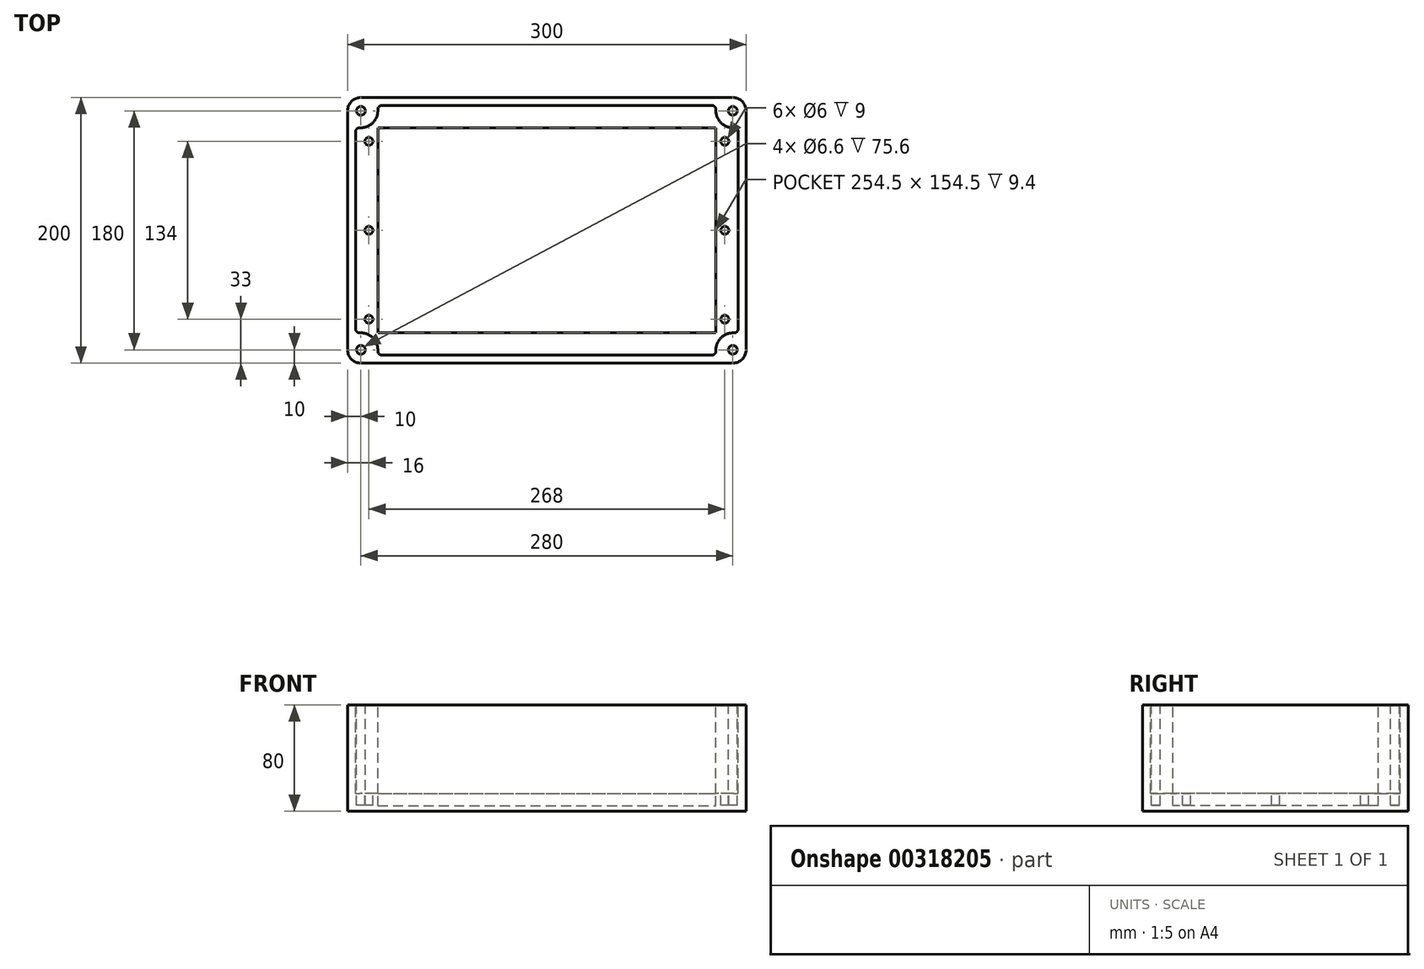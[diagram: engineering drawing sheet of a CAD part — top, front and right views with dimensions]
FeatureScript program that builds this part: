
annotation { "Feature Type Name" : "Feature", "Feature Type Description" : "" }
export const myFeature = defineFeature(function(context is Context, id is Id, definition is map)
    precondition{}
    {
        {
            var Q0;
            Q0=qCreatedBy(makeId("Top.planeOp"),FACE);
            var sketch = newSketch(context, id + "F0", { "sketchPlane" : qUnion([Q0])});
            skLineSegment(sketch, "E0.bottom", {"start": v(10, 0) * mm, "end": v(290, 0) * mm});
            skLineSegment(sketch, "E0.top", {"start": v(10, -200) * mm, "end": v(290, -200) * mm});
            skLineSegment(sketch, "E0.left", {"start": v(0, -10) * mm, "end": v(0, -190) * mm});
            skLineSegment(sketch, "E0.right", {"start": v(300, -10) * mm, "end": v(300, -190) * mm});
            skLineSegment(sketch, "E1.bottom", {"start": v(10, -10) * mm, "end": v(290, -10) * mm, "construction": true});
            skLineSegment(sketch, "E1.top", {"start": v(10, -190) * mm, "end": v(290, -190) * mm, "construction": true});
            skLineSegment(sketch, "E1.left", {"start": v(10, -10) * mm, "end": v(10, -190) * mm, "construction": true});
            skLineSegment(sketch, "E1.right", {"start": v(290, -10) * mm, "end": v(290, -190) * mm, "construction": true});
            skPoint(sketch, "E2.visualSharp", {"position": v(0, 0) * mm});
            skArc(sketch, "E2.filletArc", {"start": v(10, 0) * mm, "mid": v(2.93, -2.93) * mm, "end": v(0, -10) * mm});
            skPoint(sketch, "E3.visualSharp", {"position": v(300, 0) * mm});
            skArc(sketch, "E3.filletArc", {"start": v(300, -10) * mm, "mid": v(297.07, -2.93) * mm, "end": v(290, 0) * mm});
            skPoint(sketch, "E4.visualSharp", {"position": v(300, -200) * mm});
            skArc(sketch, "E4.filletArc", {"start": v(290, -200) * mm, "mid": v(297.07, -197.07) * mm, "end": v(300, -190) * mm});
            skPoint(sketch, "E5.visualSharp", {"position": v(0, -200) * mm});
            skArc(sketch, "E5.filletArc", {"start": v(0, -190) * mm, "mid": v(2.93, -197.07) * mm, "end": v(10, -200) * mm});
            skSolve(sketch);
        }
        {
            var Q0;
            Q0=makeQuery(id+"F0.imprint","IMPRINT",FACE,{"disambiguationData":[TD([[makeQuery(id+"F0.imprint","IMPRINT",EDGE,{"derivedFrom":sQuery(id+"F0.wireOp",EDGE,"E0.bottom")}),-1.0]])]});
            extrude(context, id + "F1", {"entities" : qUnion([Q0]), "depth" : 80 * mm});
        }
        {
            var Q0;
            Q0=makeQuery(id+"F1.opExtrude","CAP_FACE",FACE,{"disambiguationData":[OSD([sQuery(id+"F0.wireOp",EDGE,"E0.bottom"),sQuery(id+"F0.wireOp",EDGE,"E0.top"),sQuery(id+"F0.wireOp",EDGE,"E0.left"),sQuery(id+"F0.wireOp",EDGE,"E0.right")])],"isStart":false});
            var sketch = newSketch(context, id + "F2", { "sketchPlane" : qUnion([Q0])});
            skLineSegment(sketch, "E6.bottom", {"start": v(10, -10) * mm, "end": v(290, -10) * mm, "construction": true});
            skLineSegment(sketch, "E6.top", {"start": v(10, -190) * mm, "end": v(290, -190) * mm, "construction": true});
            skLineSegment(sketch, "E6.left", {"start": v(10, -10) * mm, "end": v(10, -190) * mm, "construction": true});
            skLineSegment(sketch, "E6.right", {"start": v(290, -10) * mm, "end": v(290, -190) * mm, "construction": true});
            skCircle(sketch, "E7", {"center": v(10, -10) * mm, "radius": 3.3 * mm});
            skCircle(sketch, "E8", {"center": v(290, -10) * mm, "radius": 3.3 * mm});
            skCircle(sketch, "E9", {"center": v(290, -190) * mm, "radius": 3.3 * mm});
            skCircle(sketch, "E10", {"center": v(10, -190) * mm, "radius": 3.3 * mm});
            skLineSegment(sketch, "E11.bottom", {"start": v(6, -6) * mm, "end": v(294, -6) * mm});
            skLineSegment(sketch, "E11.top", {"start": v(6, -194) * mm, "end": v(294, -194) * mm});
            skLineSegment(sketch, "E11.left", {"start": v(6, -6) * mm, "end": v(6, -194) * mm});
            skLineSegment(sketch, "E11.right", {"start": v(294, -6) * mm, "end": v(294, -194) * mm});
            skLineSegment(sketch, "E12.bottom", {"start": v(16, -33) * mm, "end": v(284, -33) * mm, "construction": true});
            skLineSegment(sketch, "E12.top", {"start": v(16, -167) * mm, "end": v(284, -167) * mm, "construction": true});
            skLineSegment(sketch, "E12.left", {"start": v(16, -33) * mm, "end": v(16, -167) * mm, "construction": true});
            skLineSegment(sketch, "E12.right", {"start": v(284, -33) * mm, "end": v(284, -167) * mm, "construction": true});
            skLineSegment(sketch, "E13", {"start": v(16, -100) * mm, "end": v(284, -100) * mm, "construction": true});
            skCircle(sketch, "E14", {"center": v(16, -33) * mm, "radius": 3 * mm});
            skCircle(sketch, "E15", {"center": v(16, -100) * mm, "radius": 3 * mm});
            skCircle(sketch, "E16", {"center": v(16, -167) * mm, "radius": 3 * mm});
            skCircle(sketch, "E17", {"center": v(284, -33) * mm, "radius": 3 * mm});
            skCircle(sketch, "E18", {"center": v(284, -100) * mm, "radius": 3 * mm});
            skCircle(sketch, "E19", {"center": v(284, -167) * mm, "radius": 3 * mm});
            skSolve(sketch);
        }
        {
            var Q0;
            Q0=makeQuery(id+"F2.imprint","IMPRINT",FACE,{"disambiguationData":[TD([[makeQuery(id+"F2.imprint","IMPRINT",EDGE,{"derivedFrom":sQuery(id+"F2.wireOp",EDGE,"E7")}),1.0]])]});
            var Q1;
            Q1=makeQuery(id+"F2.imprint","IMPRINT",FACE,{"disambiguationData":[TD([[makeQuery(id+"F2.imprint","IMPRINT",EDGE,{"derivedFrom":sQuery(id+"F2.wireOp",EDGE,"E10")}),1.0]])]});
            var Q2;
            Q2=makeQuery(id+"F2.imprint","IMPRINT",FACE,{"disambiguationData":[TD([[makeQuery(id+"F2.imprint","IMPRINT",EDGE,{"derivedFrom":sQuery(id+"F2.wireOp",EDGE,"E9")}),1.0]])]});
            var Q3;
            Q3=makeQuery(id+"F2.imprint","IMPRINT",FACE,{"disambiguationData":[TD([[makeQuery(id+"F2.imprint","IMPRINT",EDGE,{"derivedFrom":sQuery(id+"F2.wireOp",EDGE,"E8")}),1.0]])]});
            var Q4;
            Q4=makeQuery(id+"F2.imprint","IMPRINT",FACE,{"disambiguationData":[TD([[makeQuery(id+"F2.imprint","IMPRINT",EDGE,{"derivedFrom":sQuery(id+"F2.wireOp",EDGE,"E14")}),1.0]])]});
            var Q5;
            Q5=makeQuery(id+"F2.imprint","IMPRINT",FACE,{"disambiguationData":[TD([[makeQuery(id+"F2.imprint","IMPRINT",EDGE,{"derivedFrom":sQuery(id+"F2.wireOp",EDGE,"E15")}),1.0]])]});
            var Q6;
            Q6=makeQuery(id+"F2.imprint","IMPRINT",FACE,{"disambiguationData":[TD([[makeQuery(id+"F2.imprint","IMPRINT",EDGE,{"derivedFrom":sQuery(id+"F2.wireOp",EDGE,"E16")}),1.0]])]});
            var Q7;
            Q7=makeQuery(id+"F2.imprint","IMPRINT",FACE,{"disambiguationData":[TD([[makeQuery(id+"F2.imprint","IMPRINT",EDGE,{"derivedFrom":sQuery(id+"F2.wireOp",EDGE,"E18")}),1.0]])]});
            var Q8;
            Q8=makeQuery(id+"F2.imprint","IMPRINT",FACE,{"disambiguationData":[TD([[makeQuery(id+"F2.imprint","IMPRINT",EDGE,{"derivedFrom":sQuery(id+"F2.wireOp",EDGE,"E17")}),1.0]])]});
            var Q9;
            Q9=makeQuery(id+"F2.imprint","IMPRINT",FACE,{"disambiguationData":[TD([[makeQuery(id+"F2.imprint","IMPRINT",EDGE,{"derivedFrom":sQuery(id+"F2.wireOp",EDGE,"E19")}),1.0]])]});
            var Q10;
            Q10=sQuery(id+"F2.wireOp",EDGE,"E17");
            var Q11;
            Q11=sQuery(id+"F2.wireOp",EDGE,"E8");
            var Q12;
            Q12=sQuery(id+"F2.wireOp",EDGE,"E18");
            var Q13;
            Q13=sQuery(id+"F2.wireOp",EDGE,"E19");
            var Q14;
            Q14=sQuery(id+"F2.wireOp",EDGE,"E9");
            var Q15;
            Q15=sQuery(id+"F2.wireOp",EDGE,"E16");
            var Q16;
            Q16=sQuery(id+"F2.wireOp",EDGE,"E10");
            var Q17;
            Q17=sQuery(id+"F2.wireOp",EDGE,"E15");
            var Q18;
            Q18=sQuery(id+"F2.wireOp",EDGE,"E14");
            var Q19;
            Q19=sQuery(id+"F2.wireOp",EDGE,"E7");
            extrude(context, id + "F3", {"entities" : qUnion([Q0, Q1, Q2, Q3, Q4, Q5, Q6, Q7, Q8, Q9]), "operationType" : NewBodyOperationType.REMOVE, "surfaceEntities" : qUnion([Q10, Q11, Q12, Q13, Q14, Q15, Q16, Q17, Q18, Q19]), "oppositeDirection" : true, "depth" : 75.6 * mm});
        }
        {
            var Q0;
            Q0=makeQuery(id+"F1.opExtrude","CAP_FACE",FACE,{"disambiguationData":[OSD([sQuery(id+"F0.wireOp",EDGE,"E0.bottom"),sQuery(id+"F0.wireOp",EDGE,"E0.top"),sQuery(id+"F0.wireOp",EDGE,"E0.left"),sQuery(id+"F0.wireOp",EDGE,"E0.right"),sQuery(id+"F0.wireOp",EDGE,"E2.filletArc"),sQuery(id+"F0.wireOp",EDGE,"E3.filletArc"),sQuery(id+"F0.wireOp",EDGE,"E4.filletArc"),sQuery(id+"F0.wireOp",EDGE,"E5.filletArc")])],"isStart":false});
            var sketch = newSketch(context, id + "F4", { "sketchPlane" : qUnion([Q0])});
            skLineSegment(sketch, "E20.bottom", {"start": v(22.76, -22.75) * mm, "end": v(277.26, -22.75) * mm});
            skLineSegment(sketch, "E20.top", {"start": v(22.76, -177.25) * mm, "end": v(277.26, -177.25) * mm});
            skLineSegment(sketch, "E20.left", {"start": v(22.76, -22.75) * mm, "end": v(22.76, -177.25) * mm});
            skLineSegment(sketch, "E20.right", {"start": v(277.26, -22.75) * mm, "end": v(277.26, -177.25) * mm});
            skLineSegment(sketch, "E21.bottom", {"start": v(25.72, -6) * mm, "end": v(274.29, -6) * mm});
            skLineSegment(sketch, "E21.top", {"start": v(25.72, -194) * mm, "end": v(274.29, -194) * mm});
            skLineSegment(sketch, "E21.left", {"start": v(6, -25.72) * mm, "end": v(6, -174.28) * mm});
            skLineSegment(sketch, "E21.right", {"start": v(294, -25.71) * mm, "end": v(294, -174.29) * mm});
            skArc(sketch, "E22", {"start": v(9.2, -22.73) * mm, "mid": v(19.02, -19.02) * mm, "end": v(22.73, -9.2) * mm});
            skArc(sketch, "E23.filletArc", {"start": v(25.72, -6) * mm, "mid": v(23.54, -6.95) * mm, "end": v(22.73, -9.2) * mm});
            skArc(sketch, "E24.filletArc", {"start": v(9.2, -22.73) * mm, "mid": v(6.95, -23.54) * mm, "end": v(6, -25.72) * mm});
            skArc(sketch, "E25", {"start": v(277.28, -9.2) * mm, "mid": v(280.99, -19.01) * mm, "end": v(290.8, -22.72) * mm});
            skArc(sketch, "E26", {"start": v(22.73, -190.8) * mm, "mid": v(19.02, -180.98) * mm, "end": v(9.2, -177.27) * mm});
            skArc(sketch, "E27.filletArc", {"start": v(6, -174.28) * mm, "mid": v(6.95, -176.46) * mm, "end": v(9.2, -177.27) * mm});
            skArc(sketch, "E28.filletArc", {"start": v(22.73, -190.8) * mm, "mid": v(23.54, -193.05) * mm, "end": v(25.72, -194) * mm});
            skPoint(sketch, "E29.center.orphan", {"position": v(290, -186.7) * mm});
            skArc(sketch, "E30", {"start": v(290.8, -177.28) * mm, "mid": v(280.99, -180.99) * mm, "end": v(277.28, -190.8) * mm});
            skArc(sketch, "E31.filletArc", {"start": v(274.29, -194) * mm, "mid": v(276.48, -193.05) * mm, "end": v(277.28, -190.8) * mm});
            skArc(sketch, "E32.filletArc", {"start": v(290.8, -177.28) * mm, "mid": v(293.05, -176.48) * mm, "end": v(294, -174.29) * mm});
            skArc(sketch, "E33.filletArc", {"start": v(277.28, -9.2) * mm, "mid": v(276.48, -6.95) * mm, "end": v(274.29, -6) * mm});
            skArc(sketch, "E34.filletArc", {"start": v(294, -25.71) * mm, "mid": v(293.05, -23.52) * mm, "end": v(290.8, -22.72) * mm});
            skSolve(sketch);
        }
        {
            var Q0;
            Q0=makeQuery(id+"F4.imprint","IMPRINT",FACE,{"disambiguationData":[TD([[makeQuery(id+"F4.imprint","IMPRINT",EDGE,{"derivedFrom":sQuery(id+"F4.wireOp",EDGE,"E20.bottom")}),1.0]])]});
            var Q1;
            Q1=makeQuery(id+"F4.imprint","IMPRINT",FACE,{"disambiguationData":[TD([[makeQuery(id+"F4.imprint","IMPRINT",EDGE,{"derivedFrom":sQuery(id+"F4.wireOp",EDGE,"E20.bottom")}),-1.0]])]});
            extrude(context, id + "F5", {"entities" : qUnion([Q0, Q1]), "operationType" : NewBodyOperationType.REMOVE, "oppositeDirection" : true, "depth" : 66.6 * mm});
        }
        {
            var Q0;
            Q0=makeQuery(id+"F5.boolean.opBoolean","COPY",FACE,{"derivedFrom":makeQuery(id+"F5.opExtrude","CAP_FACE",FACE,{"disambiguationData":[OSD([sQuery(id+"F2.wireOp",EDGE,"E14"),sQuery(id+"F2.wireOp",EDGE,"E15"),sQuery(id+"F2.wireOp",EDGE,"E16"),sQuery(id+"F2.wireOp",EDGE,"E17"),sQuery(id+"F2.wireOp",EDGE,"E18"),sQuery(id+"F2.wireOp",EDGE,"E19"),sQuery(id+"F4.wireOp",EDGE,"E21.bottom"),sQuery(id+"F4.wireOp",EDGE,"E21.top"),sQuery(id+"F4.wireOp",EDGE,"E21.left"),sQuery(id+"F4.wireOp",EDGE,"E21.right"),sQuery(id+"F4.wireOp",EDGE,"E22"),sQuery(id+"F4.wireOp",EDGE,"E23.filletArc"),sQuery(id+"F4.wireOp",EDGE,"E24.filletArc"),sQuery(id+"F4.wireOp",EDGE,"E25"),sQuery(id+"F4.wireOp",EDGE,"E26"),sQuery(id+"F4.wireOp",EDGE,"E27.filletArc"),sQuery(id+"F4.wireOp",EDGE,"E28.filletArc"),sQuery(id+"F4.wireOp",EDGE,"E30"),sQuery(id+"F4.wireOp",EDGE,"E31.filletArc"),sQuery(id+"F4.wireOp",EDGE,"E32.filletArc"),sQuery(id+"F4.wireOp",EDGE,"E33.filletArc"),sQuery(id+"F4.wireOp",EDGE,"E34.filletArc")])],"isStart":false})});
            var sketch = newSketch(context, id + "F6", { "sketchPlane" : qUnion([Q0])});
            skLineSegment(sketch, "E35.bottom", {"start": v(22.75, -22.75) * mm, "end": v(277.25, -22.75) * mm});
            skLineSegment(sketch, "E35.top", {"start": v(22.75, -177.25) * mm, "end": v(277.25, -177.25) * mm});
            skLineSegment(sketch, "E35.left", {"start": v(22.75, -22.75) * mm, "end": v(22.75, -177.25) * mm});
            skLineSegment(sketch, "E35.right", {"start": v(277.25, -22.75) * mm, "end": v(277.25, -177.25) * mm});
            skSolve(sketch);
        }
        {
            var Q0;
            Q0=makeQuery(id+"F6.imprint","IMPRINT",FACE,{"disambiguationData":[TD([[makeQuery(id+"F6.imprint","IMPRINT",EDGE,{"derivedFrom":sQuery(id+"F6.wireOp",EDGE,"E35.bottom")}),-1.0]])]});
            extrude(context, id + "F7", {"entities" : qUnion([Q0]), "operationType" : NewBodyOperationType.REMOVE, "oppositeDirection" : true, "depth" : 9.4 * mm});
        }
    });
